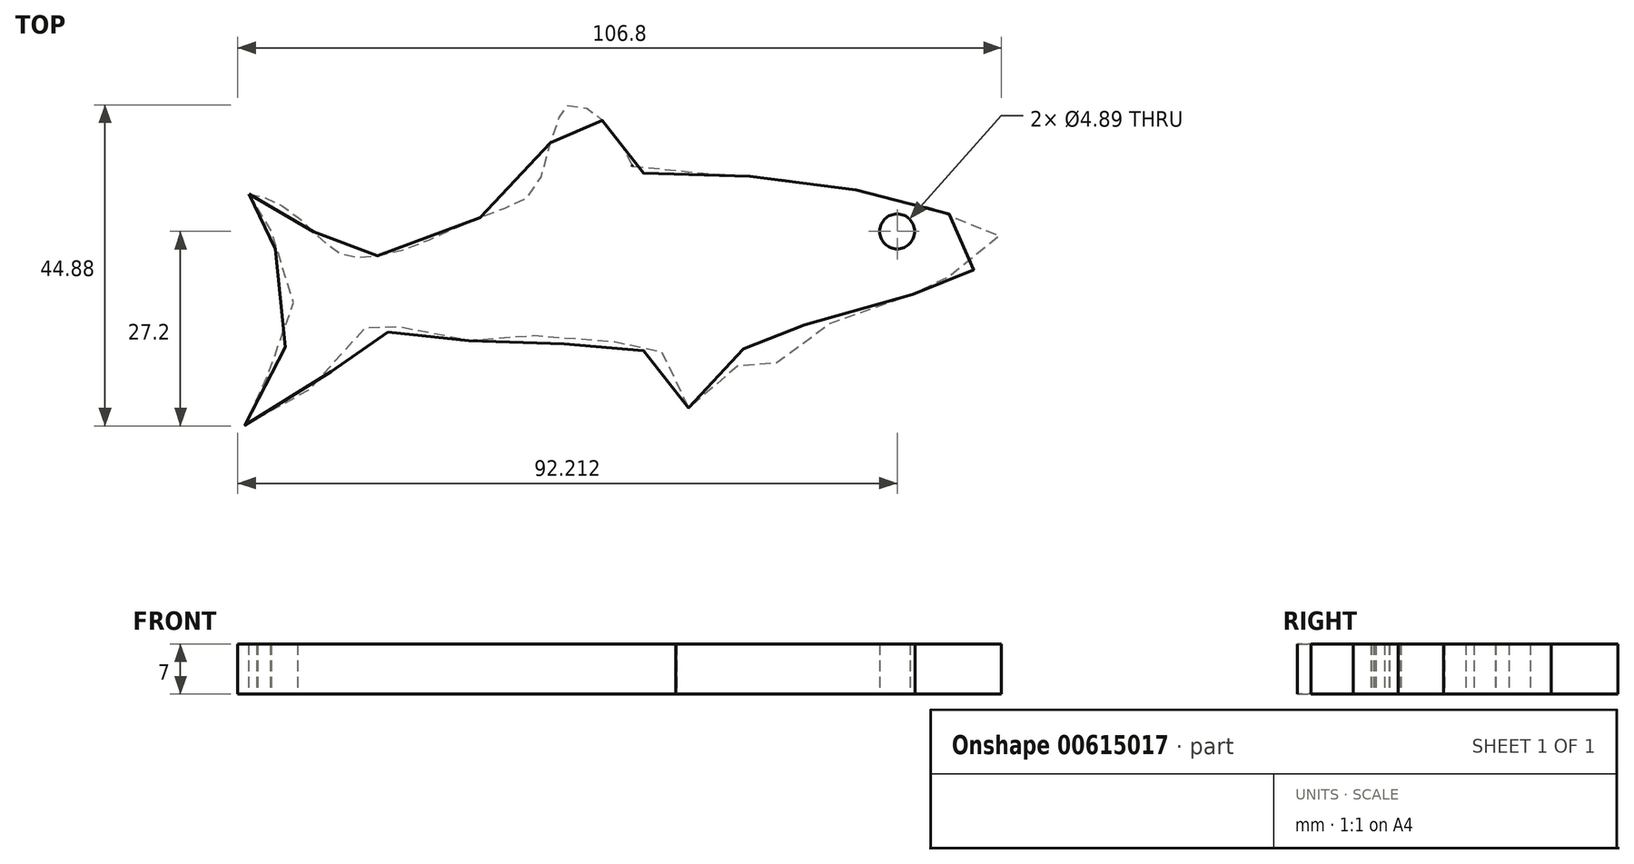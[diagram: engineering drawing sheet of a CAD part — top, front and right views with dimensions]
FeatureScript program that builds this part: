
annotation { "Feature Type Name" : "Feature", "Feature Type Description" : "" }
export const myFeature = defineFeature(function(context is Context, id is Id, definition is map)
    precondition{}
    {
        {
            var Q0;
            Q0=qCreatedBy(makeId("Top.planeOp"),FACE);
            var sketch = newSketch(context, id + "F0", { "sketchPlane" : qUnion([Q0])});
            skFitSpline(sketch, "E0", {"points": [v(-47.85, 9.56) * mm, v(-46.54, 9.4) * mm, v(-43.7, 8.18) * mm, v(-41.1, 6.42) * mm, v(-39.02, 4.42) * mm, v(-36.88, 2.5) * mm, v(-35.19, 1.28) * mm, v(-33.27, 0.74) * mm, v(-31.05, 0.74) * mm, v(-26.44, 1.66) * mm, v(-20.92, 3.88) * mm, v(-16.09, 6.03) * mm, v(-10.87, 8.03) * mm, v(-7.72, 10.25) * mm, v(-5.42, 17.46) * mm, v(-3.88, 21.27) * mm, v(-3.14, 21.96) * mm, v(0, 21.3) * mm, v(1.64, 19.75) * mm, v(2.96, 17.97) * mm, v(4.53, 15.97) * mm, v(5.77, 13.48) * mm, v(6.34, 12.66) * mm, v(9.89, 12.55) * mm, v(14.83, 12.55) * mm, v(20.52, 12.14) * mm, v(25.8, 11.7) * mm, v(30.66, 11) * mm, v(36.27, 10.26) * mm, v(41.4, 9.16) * mm, v(46.86, 7.92) * mm, v(48.8, 7.05) * mm, v(53, 6.02) * mm, v(57.38, 3.1) * mm, v(55.38, 0) * mm, v(51.18, -1.82) * mm, v(45.89, -2.37) * mm, v(44.61, -2.37) * mm, v(45.34, -3.65) * mm, v(44.25, -5.1) * mm, v(38.96, -7.66) * mm, v(30.93, -8.76) * mm, v(29.1, -9.12) * mm, v(26.37, -13.68) * mm, v(23.08, -14.78) * mm, v(21.26, -12.04) * mm, v(19.98, -16.42) * mm, v(16.7, -20.25) * mm, v(14.32, -20.8) * mm, v(11.95, -17.33) * mm, v(11.95, -15.14) * mm, v(9.94, -12.59) * mm, v(7.39, -12.4) * mm, v(6.66, -10.95) * mm, v(4.29, -10.95) * mm, v(0, -11.86) * mm, v(-5.57, -10.95) * mm, v(-11.95, -10.22) * mm, v(-15.42, -12.23) * mm, v(-17.8, -10.22) * mm, v(-22.17, -8.76) * mm, v(-26.55, -8.94) * mm, v(-28, -10.04) * mm, v(-28.92, -8.94) * mm, v(-29.47, -8.4) * mm, v(-31.3, -8.94) * mm, v(-34.03, -12.77) * mm, v(-38.62, -17.24) * mm, v(-43.29, -20.5) * mm, v(-47.84, -22.88) * mm, v(-48.5, -22.78) * mm, v(-49.36, -22.45) * mm, v(-47.2, -19.09) * mm, v(-44.37, -14.31) * mm, v(-41.12, -8.78) * mm, v(-41.55, -5.74) * mm, v(-43.18, 0) * mm, v(-44.8, 3.8) * mm, v(-44.8, 4.78) * mm, v(-46.65, 4.9) * mm, v(-46.65, 6.2) * mm, v(-47.85, 9.56) * mm]});
            skCircle(sketch, "E1", {"center": v(42.83, 4.31) * mm, "radius": 2.44 * mm});
            skSolve(sketch);
        }
        {
            var Q0;
            Q0=makeQuery(id+"F0.imprint","IMPRINT",FACE,{"disambiguationData":[TD([[makeQuery(id+"F0.imprint","IMPRINT",EDGE,{"derivedFrom":sQuery(id+"F0.wireOp",EDGE,"E0")}),-1.0]])]});
            extrude(context, id + "F1", {"entities" : qUnion([Q0]), "depth" : 7 * mm, "offsetDistance" : 25 * mm});
        }
    });
